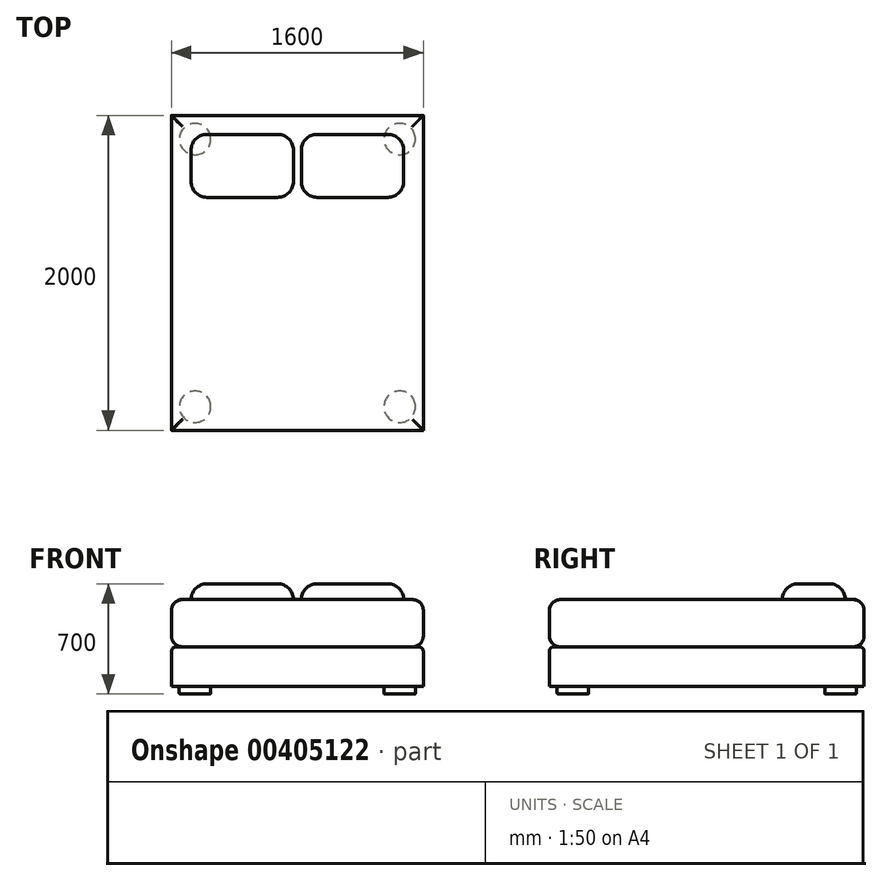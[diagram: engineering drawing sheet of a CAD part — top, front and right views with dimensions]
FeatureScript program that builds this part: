
annotation { "Feature Type Name" : "Feature", "Feature Type Description" : "" }
export const myFeature = defineFeature(function(context is Context, id is Id, definition is map)
    precondition{}
    {
        {
            assignVariable(context, id + "F0", {"name" : "raio", "anyValue" : 0.1});
        }
        {
            var Q0;
            Q0=qCreatedBy(makeId("Top.planeOp"),FACE);
            var sketch = newSketch(context, id + "F1", { "sketchPlane" : qUnion([Q0])});
            skLineSegment(sketch, "E0.bottom", {"start": v(-800, 1000) * mm, "end": v(800, 1000) * mm});
            skLineSegment(sketch, "E0.top", {"start": v(-800, -1000) * mm, "end": v(800, -1000) * mm});
            skLineSegment(sketch, "E0.left", {"start": v(-800, 1000) * mm, "end": v(-800, -1000) * mm});
            skLineSegment(sketch, "E0.right", {"start": v(800, 1000) * mm, "end": v(800, -1000) * mm});
            skLineSegment(sketch, "E1", {"start": v(0, -618.18) * mm, "end": v(0, 618.18) * mm, "construction": true});
            skLineSegment(sketch, "E2", {"start": v(-494.55, 0) * mm, "end": v(494.55, 0) * mm, "construction": true});
            skCircle(sketch, "E3", {"center": v(-650, 850) * mm, "radius": 100 * mm});
            skCircle(sketch, "E4", {"center": v(650, 850) * mm, "radius": 100 * mm});
            skCircle(sketch, "E5", {"center": v(-650, -850) * mm, "radius": 100 * mm});
            skCircle(sketch, "E6", {"center": v(650, -850) * mm, "radius": 100 * mm});
            skSolve(sketch);
        }
        {
            var Q0;
            Q0=qSketchRegion(id+"F1",true);
            var Q1;
            Q1=makeQuery(id+"F1.imprint","IMPRINT",FACE,{"disambiguationData":[TD([[makeQuery(id+"F1.imprint","IMPRINT",EDGE,{"derivedFrom":sQuery(id+"F1.wireOp",EDGE,"E5")}),1.0]])]});
            var Q2;
            Q2=makeQuery(id+"F1.imprint","IMPRINT",FACE,{"disambiguationData":[TD([[makeQuery(id+"F1.imprint","IMPRINT",EDGE,{"derivedFrom":sQuery(id+"F1.wireOp",EDGE,"E3")}),1.0]])]});
            var Q3;
            Q3=makeQuery(id+"F1.imprint","IMPRINT",FACE,{"disambiguationData":[TD([[makeQuery(id+"F1.imprint","IMPRINT",EDGE,{"derivedFrom":sQuery(id+"F1.wireOp",EDGE,"E4")}),1.0]])]});
            var Q4;
            Q4=makeQuery(id+"F1.imprint","IMPRINT",FACE,{"disambiguationData":[TD([[makeQuery(id+"F1.imprint","IMPRINT",EDGE,{"derivedFrom":sQuery(id+"F1.wireOp",EDGE,"E6")}),1.0]])]});
            extrude(context, id + "F2", {"entities" : qUnion([Q0, Q1, Q2, Q3, Q4]), "depth" : 300 * mm, "hasSecondDirection" : true, "secondDirectionOppositeDirection" : false, "secondDirectionDepth" : 50 * mm});
        }
        {
            var Q0;
            Q0=makeQuery(id+"F1.imprint","IMPRINT",FACE,{"disambiguationData":[TD([[makeQuery(id+"F1.imprint","IMPRINT",EDGE,{"derivedFrom":sQuery(id+"F1.wireOp",EDGE,"E5")}),1.0]])]});
            var Q1;
            Q1=makeQuery(id+"F1.imprint","IMPRINT",FACE,{"disambiguationData":[TD([[makeQuery(id+"F1.imprint","IMPRINT",EDGE,{"derivedFrom":sQuery(id+"F1.wireOp",EDGE,"E6")}),1.0]])]});
            var Q2;
            Q2=makeQuery(id+"F1.imprint","IMPRINT",FACE,{"disambiguationData":[TD([[makeQuery(id+"F1.imprint","IMPRINT",EDGE,{"derivedFrom":sQuery(id+"F1.wireOp",EDGE,"E3")}),1.0]])]});
            var Q3;
            Q3=makeQuery(id+"F1.imprint","IMPRINT",FACE,{"disambiguationData":[TD([[makeQuery(id+"F1.imprint","IMPRINT",EDGE,{"derivedFrom":sQuery(id+"F1.wireOp",EDGE,"E4")}),1.0]])]});
            extrude(context, id + "F3", {"entities" : qUnion([Q0, Q1, Q2, Q3]), "operationType" : NewBodyOperationType.ADD, "endBound" : BoundingType.UP_TO_NEXT, "depth" : 25 * mm});
        }
        {
            var Q0;
            Q0=makeQuery(id+"F2.opExtrude","SWEPT_EDGE",EDGE,{"disambiguationData":[OSD([sQuery(id+"F1.wireOp",EDGE,"E0.top"),sQuery(id+"F1.wireOp",EDGE,"E0.right")])]});
            var Q1;
            Q1=makeQuery(id+"F2.opExtrude","SWEPT_EDGE",EDGE,{"disambiguationData":[OSD([sQuery(id+"F1.wireOp",EDGE,"E0.bottom"),sQuery(id+"F1.wireOp",EDGE,"E0.right")])]});
            var Q2;
            Q2=makeQuery(id+"F2.opExtrude","SWEPT_EDGE",EDGE,{"disambiguationData":[OSD([sQuery(id+"F1.wireOp",EDGE,"E0.top"),sQuery(id+"F1.wireOp",EDGE,"E0.left")])]});
            var Q3;
            Q3=makeQuery(id+"F2.opExtrude","SWEPT_EDGE",EDGE,{"disambiguationData":[OSD([sQuery(id+"F1.wireOp",EDGE,"E0.bottom"),sQuery(id+"F1.wireOp",EDGE,"E0.left")])]});
            fillet(context, id + "F4", {"entities" : qUnion([Q0, Q1, Q2, Q3]), "radius" : (getVariable(context, 'raio')) * mm, "tangentPropagation" : true, "allowEdgeOverflow" : false});
        }
        {
            var Q0;
            Q0=makeQuery(id+"F2.opExtrude","CAP_EDGE",EDGE,{"disambiguationData":[OSD([sQuery(id+"F1.wireOp",EDGE,"E0.right")])],"isStart":false});
            var Q1;
            Q1=makeQuery(id+"F2.opExtrude","CAP_EDGE",EDGE,{"disambiguationData":[OSD([sQuery(id+"F1.wireOp",EDGE,"E0.top")])],"isStart":false});
            var Q2;
            Q2=makeQuery(id+"F2.opExtrude","CAP_EDGE",EDGE,{"disambiguationData":[OSD([sQuery(id+"F1.wireOp",EDGE,"E0.left")])],"isStart":false});
            var Q3;
            Q3=makeQuery(id+"F2.opExtrude","CAP_EDGE",EDGE,{"disambiguationData":[OSD([sQuery(id+"F1.wireOp",EDGE,"E0.bottom")])],"isStart":false});
            fillet(context, id + "F5", {"entities" : qUnion([Q0, Q1, Q2, Q3]), "radius" : 30 * mm, "tangentPropagation" : true, "allowEdgeOverflow" : false});
        }
        {
            var Q0;
            Q0=makeQuery(id+"F1.imprint","IMPRINT",FACE,{"disambiguationData":[TD([[makeQuery(id+"F1.imprint","IMPRINT",EDGE,{"derivedFrom":sQuery(id+"F1.wireOp",EDGE,"E0.bottom")}),-1.0]])]});
            var Q1;
            Q1=makeQuery(id+"F1.imprint","IMPRINT",FACE,{"disambiguationData":[TD([[makeQuery(id+"F1.imprint","IMPRINT",EDGE,{"derivedFrom":sQuery(id+"F1.wireOp",EDGE,"E5")}),1.0]])]});
            var Q2;
            Q2=makeQuery(id+"F1.imprint","IMPRINT",FACE,{"disambiguationData":[TD([[makeQuery(id+"F1.imprint","IMPRINT",EDGE,{"derivedFrom":sQuery(id+"F1.wireOp",EDGE,"E6")}),1.0]])]});
            var Q3;
            Q3=makeQuery(id+"F1.imprint","IMPRINT",FACE,{"disambiguationData":[TD([[makeQuery(id+"F1.imprint","IMPRINT",EDGE,{"derivedFrom":sQuery(id+"F1.wireOp",EDGE,"E4")}),1.0]])]});
            var Q4;
            Q4=makeQuery(id+"F1.imprint","IMPRINT",FACE,{"disambiguationData":[TD([[makeQuery(id+"F1.imprint","IMPRINT",EDGE,{"derivedFrom":sQuery(id+"F1.wireOp",EDGE,"E3")}),1.0]])]});
            var Q5;
            Q5=makeQuery(id+"F2.opExtrude","CAP_FACE",FACE,{"disambiguationData":[OSD([sQuery(id+"F1.wireOp",EDGE,"E0.bottom"),sQuery(id+"F1.wireOp",EDGE,"E0.top"),sQuery(id+"F1.wireOp",EDGE,"E0.left"),sQuery(id+"F1.wireOp",EDGE,"E0.right")])],"isStart":false});
            extrude(context, id + "F6", {"entities" : qUnion([Q0, Q1, Q2, Q3, Q4]), "depth" : 600 * mm, "hasSecondDirection" : true, "secondDirectionBound" : SecondDirectionBoundingType.UP_TO_SURFACE, "secondDirectionOppositeDirection" : false, "secondDirectionBoundEntityFace" : qUnion([Q5]), "secondDirectionDepth" : 25 * mm});
        }
        {
            var Q0;
            Q0=makeQuery(id+"F6.opExtrude","SWEPT_EDGE",EDGE,{"disambiguationData":[OSD([sQuery(id+"F1.wireOp",EDGE,"E0.bottom"),sQuery(id+"F1.wireOp",EDGE,"E0.left")])]});
            var Q1;
            Q1=makeQuery(id+"F6.opExtrude","SWEPT_EDGE",EDGE,{"disambiguationData":[OSD([sQuery(id+"F1.wireOp",EDGE,"E0.top"),sQuery(id+"F1.wireOp",EDGE,"E0.left")])]});
            var Q2;
            Q2=makeQuery(id+"F6.opExtrude","SWEPT_EDGE",EDGE,{"disambiguationData":[OSD([sQuery(id+"F1.wireOp",EDGE,"E0.bottom"),sQuery(id+"F1.wireOp",EDGE,"E0.right")])]});
            var Q3;
            Q3=makeQuery(id+"F6.opExtrude","SWEPT_EDGE",EDGE,{"disambiguationData":[OSD([sQuery(id+"F1.wireOp",EDGE,"E0.top"),sQuery(id+"F1.wireOp",EDGE,"E0.right")])]});
            fillet(context, id + "F7", {"entities" : qUnion([Q0, Q1, Q2, Q3]), "radius" : (getVariable(context, 'raio')) * mm, "tangentPropagation" : true, "allowEdgeOverflow" : false});
        }
        {
            var Q0;
            Q0=makeQuery(id+"F3.opExtrude","CAP_EDGE",EDGE,{"disambiguationData":[OSD([sQuery(id+"F1.wireOp",EDGE,"E5")])],"isStart":true});
            var Q1;
            Q1=makeQuery(id+"F3.opExtrude","CAP_EDGE",EDGE,{"disambiguationData":[OSD([sQuery(id+"F1.wireOp",EDGE,"E6")])],"isStart":true});
            var Q2;
            Q2=makeQuery(id+"F3.opExtrude","CAP_EDGE",EDGE,{"disambiguationData":[OSD([sQuery(id+"F1.wireOp",EDGE,"E4")])],"isStart":true});
            var Q3;
            Q3=makeQuery(id+"F3.opExtrude","CAP_EDGE",EDGE,{"disambiguationData":[OSD([sQuery(id+"F1.wireOp",EDGE,"E3")])],"isStart":true});
            fillet(context, id + "F8", {"entities" : qUnion([Q0, Q1, Q2, Q3]), "radius" : 5 * mm, "tangentPropagation" : true, "allowEdgeOverflow" : false});
        }
        {
            var Q0;
            {var subQ0=sQuery(id+"F1.wireOp",EDGE,"E0.top");Q0=makeQuery(id+"F6.opExtrude","TWEAK_EDGE",EDGE,{"derivedFrom":[makeQuery(id+"F1.imprint","IMPRINT",EDGE,{"derivedFrom":subQ0}),makeQuery(id+"F2.opExtrude","CAP_FACE",FACE,{"disambiguationData":[OSD([sQuery(id+"F1.wireOp",EDGE,"E0.bottom"),subQ0,sQuery(id+"F1.wireOp",EDGE,"E0.left"),sQuery(id+"F1.wireOp",EDGE,"E0.right")])],"isStart":false})]});}
            var Q1;
            Q1=makeQuery(id+"F6.opExtrude","CAP_EDGE",EDGE,{"disambiguationData":[OSD([sQuery(id+"F1.wireOp",EDGE,"E0.top")])],"isStart":false});
            var Q2;
            {var subQ0=sQuery(id+"F1.wireOp",EDGE,"E0.left");var subQ1=sQuery(id+"F1.wireOp",EDGE,"E0.top");Q2=makeQuery(id+"F7.opFillet","BLEND_EDGE",EDGE,{"blendedFrom":[makeQuery(id+"F6.opExtrude","SWEPT_EDGE",EDGE,{"disambiguationData":[OSD([subQ1,subQ0])]}),makeQuery(id+"F6.opExtrude","CAP_FACE",FACE,{"disambiguationData":[OSD([sQuery(id+"F1.wireOp",EDGE,"E0.bottom"),subQ1,subQ0,sQuery(id+"F1.wireOp",EDGE,"E0.right")])],"isStart":true})],"blendedInto":[makeQuery(id+"F6.opExtrude","CAP_FACE",FACE,{"disambiguationData":[OSD([sQuery(id+"F1.wireOp",EDGE,"E0.bottom"),subQ1,subQ0,sQuery(id+"F1.wireOp",EDGE,"E0.right")])],"isStart":true})]});}
            var Q3;
            {var subQ0=sQuery(id+"F1.wireOp",EDGE,"E0.left");var subQ1=sQuery(id+"F1.wireOp",EDGE,"E0.top");Q3=makeQuery(id+"F7.opFillet","BLEND_EDGE",EDGE,{"blendedFrom":[makeQuery(id+"F6.opExtrude","SWEPT_EDGE",EDGE,{"disambiguationData":[OSD([subQ1,subQ0])]}),makeQuery(id+"F6.opExtrude","CAP_FACE",FACE,{"disambiguationData":[OSD([sQuery(id+"F1.wireOp",EDGE,"E0.bottom"),subQ1,subQ0,sQuery(id+"F1.wireOp",EDGE,"E0.right")])],"isStart":false})],"blendedInto":[makeQuery(id+"F6.opExtrude","CAP_FACE",FACE,{"disambiguationData":[OSD([sQuery(id+"F1.wireOp",EDGE,"E0.bottom"),subQ1,subQ0,sQuery(id+"F1.wireOp",EDGE,"E0.right")])],"isStart":false})]});}
            var Q4;
            {var subQ0=sQuery(id+"F1.wireOp",EDGE,"E0.left");Q4=makeQuery(id+"F6.opExtrude","TWEAK_EDGE",EDGE,{"derivedFrom":[makeQuery(id+"F1.imprint","IMPRINT",EDGE,{"derivedFrom":subQ0}),makeQuery(id+"F2.opExtrude","CAP_FACE",FACE,{"disambiguationData":[OSD([sQuery(id+"F1.wireOp",EDGE,"E0.bottom"),sQuery(id+"F1.wireOp",EDGE,"E0.top"),subQ0,sQuery(id+"F1.wireOp",EDGE,"E0.right")])],"isStart":false})]});}
            var Q5;
            Q5=makeQuery(id+"F6.opExtrude","CAP_EDGE",EDGE,{"disambiguationData":[OSD([sQuery(id+"F1.wireOp",EDGE,"E0.left")])],"isStart":false});
            var Q6;
            {var subQ0=sQuery(id+"F1.wireOp",EDGE,"E0.left");var subQ1=sQuery(id+"F1.wireOp",EDGE,"E0.bottom");Q6=makeQuery(id+"F7.opFillet","BLEND_EDGE",EDGE,{"blendedFrom":[makeQuery(id+"F6.opExtrude","SWEPT_EDGE",EDGE,{"disambiguationData":[OSD([subQ1,subQ0])]}),makeQuery(id+"F6.opExtrude","CAP_FACE",FACE,{"disambiguationData":[OSD([subQ1,sQuery(id+"F1.wireOp",EDGE,"E0.top"),subQ0,sQuery(id+"F1.wireOp",EDGE,"E0.right")])],"isStart":true})],"blendedInto":[makeQuery(id+"F6.opExtrude","CAP_FACE",FACE,{"disambiguationData":[OSD([subQ1,sQuery(id+"F1.wireOp",EDGE,"E0.top"),subQ0,sQuery(id+"F1.wireOp",EDGE,"E0.right")])],"isStart":true})]});}
            var Q7;
            {var subQ0=sQuery(id+"F1.wireOp",EDGE,"E0.left");var subQ1=sQuery(id+"F1.wireOp",EDGE,"E0.bottom");Q7=makeQuery(id+"F7.opFillet","BLEND_EDGE",EDGE,{"blendedFrom":[makeQuery(id+"F6.opExtrude","SWEPT_EDGE",EDGE,{"disambiguationData":[OSD([subQ1,subQ0])]}),makeQuery(id+"F6.opExtrude","CAP_FACE",FACE,{"disambiguationData":[OSD([subQ1,sQuery(id+"F1.wireOp",EDGE,"E0.top"),subQ0,sQuery(id+"F1.wireOp",EDGE,"E0.right")])],"isStart":false})],"blendedInto":[makeQuery(id+"F6.opExtrude","CAP_FACE",FACE,{"disambiguationData":[OSD([subQ1,sQuery(id+"F1.wireOp",EDGE,"E0.top"),subQ0,sQuery(id+"F1.wireOp",EDGE,"E0.right")])],"isStart":false})]});}
            var Q8;
            {var subQ0=sQuery(id+"F1.wireOp",EDGE,"E0.bottom");Q8=makeQuery(id+"F6.opExtrude","TWEAK_EDGE",EDGE,{"derivedFrom":[makeQuery(id+"F1.imprint","IMPRINT",EDGE,{"derivedFrom":subQ0}),makeQuery(id+"F2.opExtrude","CAP_FACE",FACE,{"disambiguationData":[OSD([subQ0,sQuery(id+"F1.wireOp",EDGE,"E0.top"),sQuery(id+"F1.wireOp",EDGE,"E0.left"),sQuery(id+"F1.wireOp",EDGE,"E0.right")])],"isStart":false})]});}
            var Q9;
            Q9=makeQuery(id+"F6.opExtrude","CAP_EDGE",EDGE,{"disambiguationData":[OSD([sQuery(id+"F1.wireOp",EDGE,"E0.bottom")])],"isStart":false});
            var Q10;
            {var subQ0=sQuery(id+"F1.wireOp",EDGE,"E0.right");var subQ1=sQuery(id+"F1.wireOp",EDGE,"E0.bottom");Q10=makeQuery(id+"F7.opFillet","BLEND_EDGE",EDGE,{"blendedFrom":[makeQuery(id+"F6.opExtrude","SWEPT_EDGE",EDGE,{"disambiguationData":[OSD([subQ1,subQ0])]}),makeQuery(id+"F6.opExtrude","CAP_FACE",FACE,{"disambiguationData":[OSD([subQ1,sQuery(id+"F1.wireOp",EDGE,"E0.top"),sQuery(id+"F1.wireOp",EDGE,"E0.left"),subQ0])],"isStart":true})],"blendedInto":[makeQuery(id+"F6.opExtrude","CAP_FACE",FACE,{"disambiguationData":[OSD([subQ1,sQuery(id+"F1.wireOp",EDGE,"E0.top"),sQuery(id+"F1.wireOp",EDGE,"E0.left"),subQ0])],"isStart":true})]});}
            var Q11;
            {var subQ0=sQuery(id+"F1.wireOp",EDGE,"E0.right");var subQ1=sQuery(id+"F1.wireOp",EDGE,"E0.bottom");Q11=makeQuery(id+"F7.opFillet","BLEND_EDGE",EDGE,{"blendedFrom":[makeQuery(id+"F6.opExtrude","SWEPT_EDGE",EDGE,{"disambiguationData":[OSD([subQ1,subQ0])]}),makeQuery(id+"F6.opExtrude","CAP_FACE",FACE,{"disambiguationData":[OSD([subQ1,sQuery(id+"F1.wireOp",EDGE,"E0.top"),sQuery(id+"F1.wireOp",EDGE,"E0.left"),subQ0])],"isStart":false})],"blendedInto":[makeQuery(id+"F6.opExtrude","CAP_FACE",FACE,{"disambiguationData":[OSD([subQ1,sQuery(id+"F1.wireOp",EDGE,"E0.top"),sQuery(id+"F1.wireOp",EDGE,"E0.left"),subQ0])],"isStart":false})]});}
            var Q12;
            {var subQ0=sQuery(id+"F1.wireOp",EDGE,"E0.right");Q12=makeQuery(id+"F6.opExtrude","TWEAK_EDGE",EDGE,{"derivedFrom":[makeQuery(id+"F1.imprint","IMPRINT",EDGE,{"derivedFrom":subQ0}),makeQuery(id+"F2.opExtrude","CAP_FACE",FACE,{"disambiguationData":[OSD([sQuery(id+"F1.wireOp",EDGE,"E0.bottom"),sQuery(id+"F1.wireOp",EDGE,"E0.top"),sQuery(id+"F1.wireOp",EDGE,"E0.left"),subQ0])],"isStart":false})]});}
            var Q13;
            Q13=makeQuery(id+"F6.opExtrude","CAP_EDGE",EDGE,{"disambiguationData":[OSD([sQuery(id+"F1.wireOp",EDGE,"E0.right")])],"isStart":false});
            var Q14;
            {var subQ0=sQuery(id+"F1.wireOp",EDGE,"E0.right");var subQ1=sQuery(id+"F1.wireOp",EDGE,"E0.top");Q14=makeQuery(id+"F7.opFillet","BLEND_EDGE",EDGE,{"blendedFrom":[makeQuery(id+"F6.opExtrude","SWEPT_EDGE",EDGE,{"disambiguationData":[OSD([subQ1,subQ0])]}),makeQuery(id+"F6.opExtrude","CAP_FACE",FACE,{"disambiguationData":[OSD([sQuery(id+"F1.wireOp",EDGE,"E0.bottom"),subQ1,sQuery(id+"F1.wireOp",EDGE,"E0.left"),subQ0])],"isStart":true})],"blendedInto":[makeQuery(id+"F6.opExtrude","CAP_FACE",FACE,{"disambiguationData":[OSD([sQuery(id+"F1.wireOp",EDGE,"E0.bottom"),subQ1,sQuery(id+"F1.wireOp",EDGE,"E0.left"),subQ0])],"isStart":true})]});}
            var Q15;
            {var subQ0=sQuery(id+"F1.wireOp",EDGE,"E0.right");var subQ1=sQuery(id+"F1.wireOp",EDGE,"E0.top");Q15=makeQuery(id+"F7.opFillet","BLEND_EDGE",EDGE,{"blendedFrom":[makeQuery(id+"F6.opExtrude","SWEPT_EDGE",EDGE,{"disambiguationData":[OSD([subQ1,subQ0])]}),makeQuery(id+"F6.opExtrude","CAP_FACE",FACE,{"disambiguationData":[OSD([sQuery(id+"F1.wireOp",EDGE,"E0.bottom"),subQ1,sQuery(id+"F1.wireOp",EDGE,"E0.left"),subQ0])],"isStart":false})],"blendedInto":[makeQuery(id+"F6.opExtrude","CAP_FACE",FACE,{"disambiguationData":[OSD([sQuery(id+"F1.wireOp",EDGE,"E0.bottom"),subQ1,sQuery(id+"F1.wireOp",EDGE,"E0.left"),subQ0])],"isStart":false})]});}
            fillet(context, id + "F9", {"entities" : qUnion([Q0, Q1, Q2, Q3, Q4, Q5, Q6, Q7, Q8, Q9, Q10, Q11, Q12, Q13, Q14, Q15]), "radius" : 70 * mm, "tangentPropagation" : true, "allowEdgeOverflow" : false});
        }
        {
            var Q0;
            Q0=makeQuery(id+"F6.opExtrude","CAP_FACE",FACE,{"disambiguationData":[OSD([sQuery(id+"F1.wireOp",EDGE,"E0.bottom"),sQuery(id+"F1.wireOp",EDGE,"E0.top"),sQuery(id+"F1.wireOp",EDGE,"E0.left"),sQuery(id+"F1.wireOp",EDGE,"E0.right")])],"isStart":false});
            var sketch = newSketch(context, id + "F10", { "sketchPlane" : qUnion([Q0])});
            skLineSegment(sketch, "E7.bottom", {"start": v(25, 880) * mm, "end": v(675, 880) * mm});
            skLineSegment(sketch, "E7.top", {"start": v(25, 480) * mm, "end": v(675, 480) * mm});
            skLineSegment(sketch, "E7.left", {"start": v(25, 880) * mm, "end": v(25, 480) * mm});
            skLineSegment(sketch, "E7.right", {"start": v(675, 880) * mm, "end": v(675, 480) * mm});
            skPoint(sketch, "E8.firstSnap0", {"position": v(350, 880) * mm});
            skLineSegment(sketch, "E8.bottom", {"start": v(-675, 880) * mm, "end": v(-25, 880) * mm});
            skLineSegment(sketch, "E8.top", {"start": v(-675, 480) * mm, "end": v(-25, 480) * mm});
            skLineSegment(sketch, "E8.left", {"start": v(-675, 880) * mm, "end": v(-675, 480) * mm});
            skLineSegment(sketch, "E8.right", {"start": v(-25, 880) * mm, "end": v(-25, 480) * mm});
            skLineSegment(sketch, "E9", {"start": v(0, 480) * mm, "end": v(0, 880) * mm, "construction": true});
            skSolve(sketch);
        }
        {
            var Q0;
            Q0=makeQuery(id+"F10.imprint","IMPRINT",FACE,{"disambiguationData":[TD([[makeQuery(id+"F10.imprint","IMPRINT",EDGE,{"derivedFrom":sQuery(id+"F10.wireOp",EDGE,"E8.bottom")}),-1.0]])]});
            var Q1;
            Q1=makeQuery(id+"F10.imprint","IMPRINT",FACE,{"disambiguationData":[TD([[makeQuery(id+"F10.imprint","IMPRINT",EDGE,{"derivedFrom":sQuery(id+"F10.wireOp",EDGE,"E7.bottom")}),-1.0]])]});
            extrude(context, id + "F11", {"entities" : qUnion([Q0, Q1]), "operationType" : NewBodyOperationType.ADD, "depth" : 100 * mm});
        }
        {
            var Q0;
            Q0=makeQuery(id+"F11.opExtrude","SWEPT_EDGE",EDGE,{"disambiguationData":[OSD([sQuery(id+"F10.wireOp",EDGE,"E8.top"),sQuery(id+"F10.wireOp",EDGE,"E8.left")])]});
            var Q1;
            Q1=makeQuery(id+"F11.opExtrude","SWEPT_EDGE",EDGE,{"disambiguationData":[OSD([sQuery(id+"F10.wireOp",EDGE,"E8.top"),sQuery(id+"F10.wireOp",EDGE,"E8.right")])]});
            var Q2;
            Q2=makeQuery(id+"F11.opExtrude","SWEPT_EDGE",EDGE,{"disambiguationData":[OSD([sQuery(id+"F10.wireOp",EDGE,"E7.top"),sQuery(id+"F10.wireOp",EDGE,"E7.left")])]});
            var Q3;
            Q3=makeQuery(id+"F11.opExtrude","SWEPT_EDGE",EDGE,{"disambiguationData":[OSD([sQuery(id+"F10.wireOp",EDGE,"E7.top"),sQuery(id+"F10.wireOp",EDGE,"E7.right")])]});
            var Q4;
            Q4=makeQuery(id+"F11.opExtrude","SWEPT_EDGE",EDGE,{"disambiguationData":[OSD([sQuery(id+"F10.wireOp",EDGE,"E7.bottom"),sQuery(id+"F10.wireOp",EDGE,"E7.right")])]});
            var Q5;
            Q5=makeQuery(id+"F11.opExtrude","SWEPT_EDGE",EDGE,{"disambiguationData":[OSD([sQuery(id+"F10.wireOp",EDGE,"E8.bottom"),sQuery(id+"F10.wireOp",EDGE,"E8.right")])]});
            var Q6;
            Q6=makeQuery(id+"F11.opExtrude","SWEPT_EDGE",EDGE,{"disambiguationData":[OSD([sQuery(id+"F10.wireOp",EDGE,"E7.bottom"),sQuery(id+"F10.wireOp",EDGE,"E7.left")])]});
            var Q7;
            Q7=makeQuery(id+"F11.opExtrude","SWEPT_EDGE",EDGE,{"disambiguationData":[OSD([sQuery(id+"F10.wireOp",EDGE,"E8.bottom"),sQuery(id+"F10.wireOp",EDGE,"E8.left")])]});
            fillet(context, id + "F12", {"entities" : qUnion([Q0, Q1, Q2, Q3, Q4, Q5, Q6, Q7]), "radius" : 100 * mm, "tangentPropagation" : true, "allowEdgeOverflow" : false});
        }
        {
            var Q0;
            Q0=makeQuery(id+"F11.opExtrude","CAP_EDGE",EDGE,{"disambiguationData":[OSD([sQuery(id+"F10.wireOp",EDGE,"E8.top")])],"isStart":false});
            var Q1;
            Q1=makeQuery(id+"F11.opExtrude","CAP_EDGE",EDGE,{"disambiguationData":[OSD([sQuery(id+"F10.wireOp",EDGE,"E7.top")])],"isStart":false});
            fillet(context, id + "F13", {"entities" : qUnion([Q0, Q1]), "radius" : 100 * mm, "tangentPropagation" : true, "allowEdgeOverflow" : false});
        }
    });
